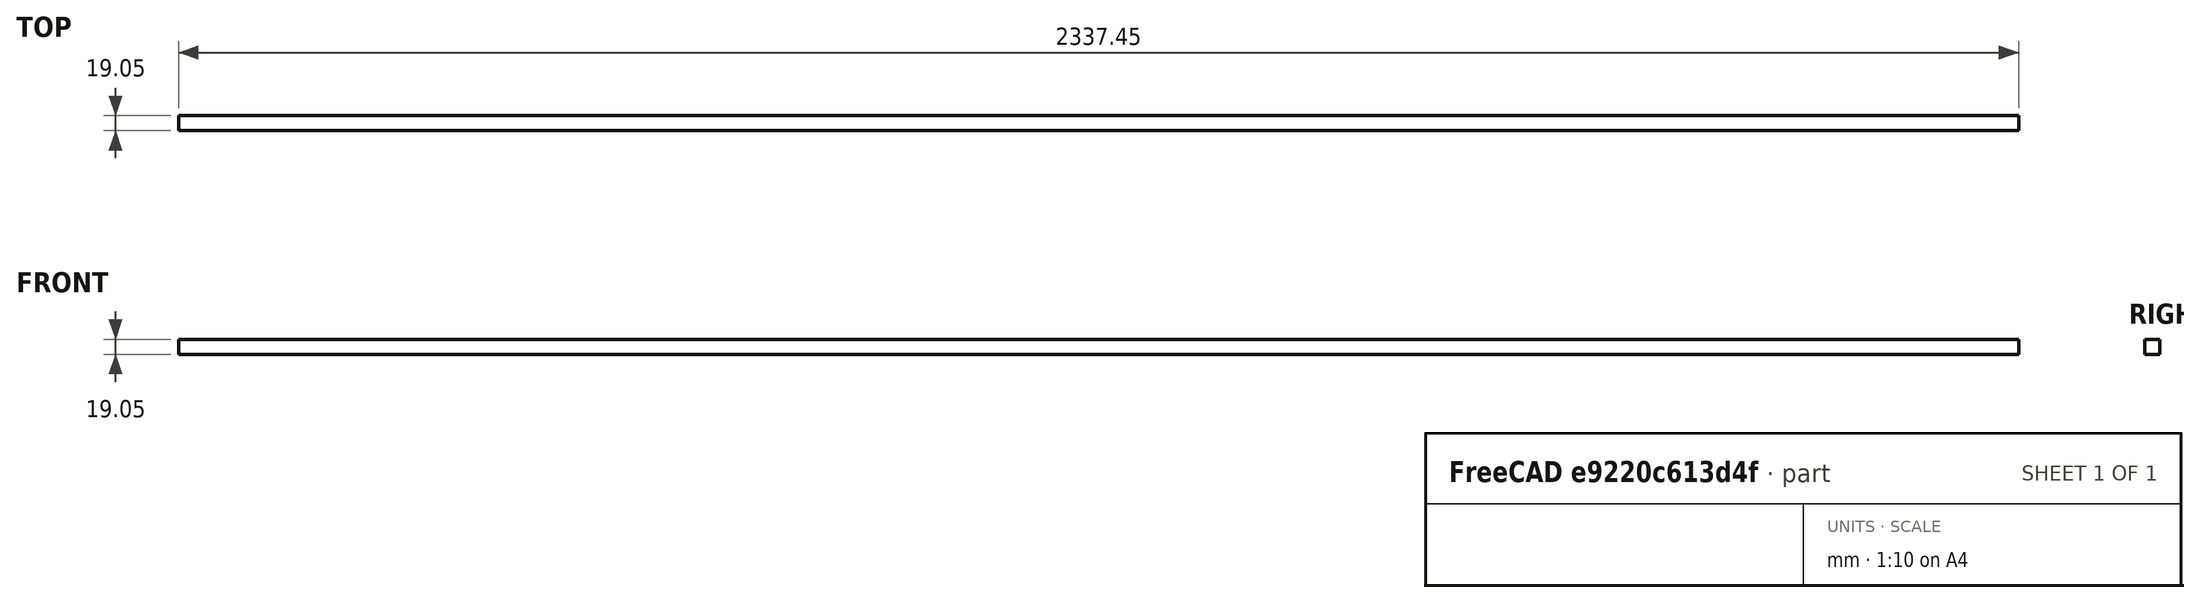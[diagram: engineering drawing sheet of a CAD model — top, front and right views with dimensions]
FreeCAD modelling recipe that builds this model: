
FCSTD DOCUMENT  (FreeCAD 0.20R29177 (Git))
Label: longStringer
License: All rights reserved
LicenseURL: http://en.wikipedia.org/wiki/All_rights_reserved
objects: Sketcher::SketchObject×1, PartDesign::Pad×1, PartDesign::Body×1
note: 4 computed .brp shape members not serialized (recipe doc carries the construction recipe); baked Part::Feature solids carry a one-line shape summary decoded from their .brp

FEATURE [Sketcher::SketchObject] Sketch
  FullyConstrained = true
  MapMode = 5
  Support = -> [XY_Plane]
  expr: Constraints[10] = 801.55 - 5 - 5 - 3 / 4 * 25.4
  expr: Constraints[9] = 3 / 4 * 25.4
  sketch-geometry (4):
    g0: LineSegment StartX=0 StartY=0 StartZ=0 EndX=772.5 EndY=0 EndZ=0
    g1: LineSegment StartX=772.5 StartY=0 StartZ=0 EndX=772.5 EndY=19.05 EndZ=0
    g2: LineSegment StartX=772.5 StartY=19.05 StartZ=0 EndX=0 EndY=19.05 EndZ=0
    g3: LineSegment StartX=0 StartY=19.05 StartZ=0 EndX=0 EndY=0 EndZ=0
  constraints (11):
    c: Coincident(g0,g1)
    c: Coincident(g1,g2)
    c: Coincident(g2,g3)
    c: Coincident(g3,g0)
    c: Horizontal(g0)
    c: Horizontal(g2)
    c: Vertical(g1)
    c: Vertical(g3)
    c: Coincident(g0,g-1)
    c: DistanceY(g3,g3) = 19.05
    c: DistanceX(g0,g0) = 772.5
FEATURE [PartDesign::Pad] Pad
  Direction = (0,0,1)
  Length = 19.05
  Length2 = 10
  Profile = -> Sketch
  ReferenceAxis = -> Sketch [N_Axis]
  Type = 0
  expr: Length = 3 / 4 * 25.4
FEATURE [PartDesign::Body] Body
  Group = -> [Sketch,Pad]
  Origin = -> Origin
  Tip = -> Pad
